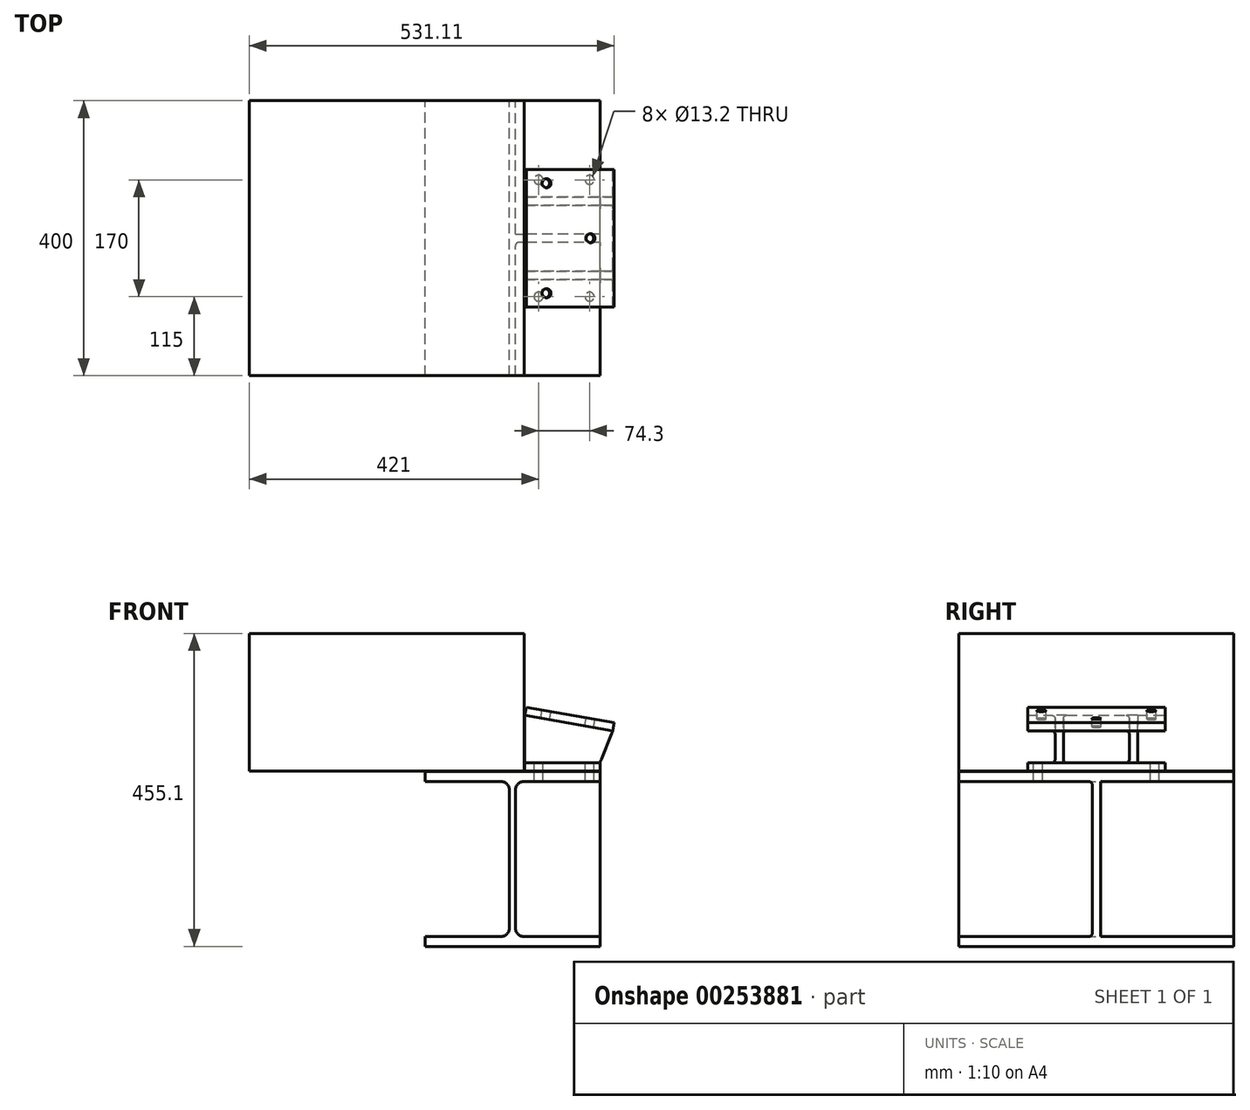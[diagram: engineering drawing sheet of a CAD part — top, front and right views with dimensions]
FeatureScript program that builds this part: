
annotation { "Feature Type Name" : "Feature", "Feature Type Description" : "" }
export const myFeature = defineFeature(function(context is Context, id is Id, definition is map)
    precondition{}
    {
        {
            var Q0;
            Q0=qCreatedBy(makeId("Front.planeOp"),FACE);
            var sketch = newSketch(context, id + "F0", { "sketchPlane" : qUnion([Q0])});
            skLineSegment(sketch, "E0.bottom", {"start": v(127.3, 127.05) * mm, "end": v(-127.3, 127.05) * mm});
            skLineSegment(sketch, "E0.top", {"start": v(127.3, -127.05) * mm, "end": v(-127.3, -127.05) * mm});
            skLineSegment(sketch, "E0.left", {"start": v(127.3, 127.05) * mm, "end": v(127.3, 112.85) * mm});
            skLineSegment(sketch, "E0.right", {"start": v(-127.3, 127.05) * mm, "end": v(-127.3, 112.85) * mm});
            skPoint(sketch, "E0.middle", {"position": v(0, 0) * mm});
            skLineSegment(sketch, "E1.0", {"start": v(127.3, 112.85) * mm, "end": v(17, 112.85) * mm});
            skLineSegment(sketch, "E2.0", {"start": v(127.3, -112.85) * mm, "end": v(17, -112.85) * mm});
            skLineSegment(sketch, "E3.0", {"start": v(4.3, 100.15) * mm, "end": v(4.3, -100.15) * mm});
            skLineSegment(sketch, "E4.0", {"start": v(-4.3, 100.15) * mm, "end": v(-4.3, -100.15) * mm});
            skLineSegment(sketch, "E5.trimOffspring", {"start": v(-17, 112.85) * mm, "end": v(-127.3, 112.85) * mm});
            skPoint(sketch, "E6.start.orphan", {"position": v(0, 127.05) * mm});
            skLineSegment(sketch, "E7.trimOffspring", {"start": v(-17, -112.85) * mm, "end": v(-127.3, -112.85) * mm});
            skPoint(sketch, "E8.trimOffspring.end.orphan", {"position": v(0, -127.05) * mm});
            skLineSegment(sketch, "E9.trimOffspring", {"start": v(-127.3, -112.85) * mm, "end": v(-127.3, -127.05) * mm});
            skLineSegment(sketch, "E10.trimOffspring", {"start": v(127.3, -112.85) * mm, "end": v(127.3, -127.05) * mm});
            skPoint(sketch, "E11.visualSharp", {"position": v(-4.3, 112.85) * mm});
            skArc(sketch, "E11.filletArc", {"start": v(-4.3, 100.15) * mm, "mid": v(-8.02, 109.13) * mm, "end": v(-17, 112.85) * mm});
            skPoint(sketch, "E12.visualSharp", {"position": v(4.3, 112.85) * mm});
            skArc(sketch, "E12.filletArc", {"start": v(17, 112.85) * mm, "mid": v(8.02, 109.13) * mm, "end": v(4.3, 100.15) * mm});
            skPoint(sketch, "E13.visualSharp", {"position": v(4.3, -112.85) * mm});
            skArc(sketch, "E13.filletArc", {"start": v(4.3, -100.15) * mm, "mid": v(8.02, -109.13) * mm, "end": v(17, -112.85) * mm});
            skPoint(sketch, "E14.visualSharp", {"position": v(-4.3, -112.85) * mm});
            skArc(sketch, "E14.filletArc", {"start": v(-17, -112.85) * mm, "mid": v(-8.02, -109.13) * mm, "end": v(-4.3, -100.15) * mm});
            skSolve(sketch);
        }
        {
            var Q0;
            Q0=makeQuery(id+"F0.imprint","IMPRINT",FACE,{"disambiguationData":[TD([[makeQuery(id+"F0.imprint","IMPRINT",EDGE,{"derivedFrom":sQuery(id+"F0.wireOp",EDGE,"E0.bottom")}),1.0]])]});
            extrude(context, id + "F1", {"entities" : qUnion([Q0]), "depth" : 400 * mm});
        }
        {
            var Q0;
            Q0=makeQuery(id+"F1.opExtrude","SWEPT_FACE",FACE,{"disambiguationData":[OSD([sQuery(id+"F0.wireOp",EDGE,"E0.bottom")])]});
            cPlane(context, id + "F2", {"entities" : qUnion([Q0]), "cplaneType" : CPlaneType.OFFSET, "offset" : 1 * mm, "width" : 150 * mm, "height" : 150 * mm});
        }
        {
            var Q0;
            Q0=qCreatedBy(id+"F2.planeOp",FACE);
            var sketch = newSketch(context, id + "F3", { "sketchPlane" : qUnion([Q0])});
            skLineSegment(sketch, "E15", {"start": v(17, 0) * mm, "end": v(17, -400) * mm});
            skLineSegment(sketch, "E16", {"start": v(17, -400) * mm, "end": v(-383, -400) * mm});
            skLineSegment(sketch, "E17", {"start": v(-383, -400) * mm, "end": v(-383, 0) * mm});
            skLineSegment(sketch, "E18", {"start": v(-383, 0) * mm, "end": v(17, 0) * mm});
            skSolve(sketch);
        }
        {
            var Q0;
            Q0=makeQuery(id+"F3.imprint","IMPRINT",FACE,{"disambiguationData":[TD([[makeQuery(id+"F3.imprint","IMPRINT",EDGE,{"derivedFrom":sQuery(id+"F3.wireOp",EDGE,"E15")}),-1.0]])]});
            extrude(context, id + "F4", {"entities" : qUnion([Q0]), "operationType" : NewBodyOperationType.ADD, "depth" : 200 * mm});
        }
        {
            var Q0;
            Q0=qCreatedBy(id+"F2.planeOp",FACE);
            var sketch = newSketch(context, id + "F5", { "sketchPlane" : qUnion([Q0])});
            skLineSegment(sketch, "E19.bottom", {"start": v(127.3, -300) * mm, "end": v(18, -300) * mm});
            skLineSegment(sketch, "E19.top", {"start": v(127.3, -100) * mm, "end": v(18, -100) * mm});
            skLineSegment(sketch, "E19.left", {"start": v(127.3, -300) * mm, "end": v(127.3, -100) * mm});
            skLineSegment(sketch, "E19.right", {"start": v(18, -300) * mm, "end": v(18, -100) * mm});
            skSolve(sketch);
        }
        {
            var Q0;
            Q0=makeQuery(id+"F5.imprint","IMPRINT",FACE,{"disambiguationData":[TD([[makeQuery(id+"F5.imprint","IMPRINT",EDGE,{"derivedFrom":sQuery(id+"F5.wireOp",EDGE,"E19.bottom")}),-1.0]])]});
            extrude(context, id + "F6", {"entities" : qUnion([Q0]), "depth" : 12 * mm});
        }
        {
            var Q0;
            Q0=makeQuery(id+"F6.opExtrude","CAP_FACE",FACE,{"disambiguationData":[OSD([sQuery(id+"F5.wireOp",EDGE,"E19.bottom"),sQuery(id+"F5.wireOp",EDGE,"E19.top"),sQuery(id+"F5.wireOp",EDGE,"E19.left"),sQuery(id+"F5.wireOp",EDGE,"E19.right")])],"isStart":false});
            var sketch = newSketch(context, id + "F7", { "sketchPlane" : qUnion([Q0])});
            skPoint(sketch, "E20", {"position": v(38, -285) * mm});
            skPoint(sketch, "E21", {"position": v(112.3, -115) * mm});
            skPoint(sketch, "E22", {"position": v(112.3, -285) * mm});
            skPoint(sketch, "E23", {"position": v(38, -115) * mm});
            skSolve(sketch);
        }
        {
            var Q0;
            Q0=sQuery(id+"F7.wireOp",VERTEX,"E20");
            var Q1;
            Q1=sQuery(id+"F7.wireOp",VERTEX,"E22");
            var Q2;
            Q2=sQuery(id+"F7.wireOp",VERTEX,"E23");
            var Q3;
            Q3=sQuery(id+"F7.wireOp",VERTEX,"E21");
            var Q4;
            Q4=makeQuery(id+"F6.opExtrude","SWEPT_BODY",BODY,{"disambiguationData":[OSD([sQuery(id+"F5.wireOp",EDGE,"E19.bottom"),sQuery(id+"F5.wireOp",EDGE,"E19.top"),sQuery(id+"F5.wireOp",EDGE,"E19.left"),sQuery(id+"F5.wireOp",EDGE,"E19.right")])]});
            hole(context, id + "F8", {"style" : HoleStyle.SIMPLE, "endStyle" : HoleEndStyle.BLIND, "standardTappedOrClearance" : lookupTablePath({ "standard" : "ISO", "fit" : "Normal", "size" : "M12", "type" : "Clearance" }), "standardBlindInLast" : lookupTablePath({ "fit" : "Standard", "standard" : "ISO", "size" : "M12", "type" : "Clearance" }), "holeDiameter" : 13.2 * mm, "holeDepth" : 12 * mm, "tappedDepth" : 12 * mm, "tapClearance" : 3, "locations" : qUnion([Q0, Q1, Q2, Q3]), "scope" : qUnion([Q4])});
        }
        {
            var Q0;
            Q0=makeQuery(id+"F1.opExtrude","SWEPT_FACE",FACE,{"disambiguationData":[OSD([sQuery(id+"F0.wireOp",EDGE,"E0.bottom")])]});
            var sketch = newSketch(context, id + "F9", { "sketchPlane" : qUnion([Q0])});
            skPoint(sketch, "E24", {"position": v(38, -285) * mm});
            skPoint(sketch, "E25", {"position": v(112.3, -285) * mm});
            skPoint(sketch, "E26", {"position": v(112.3, -115) * mm});
            skPoint(sketch, "E27", {"position": v(38, -115) * mm});
            skSolve(sketch);
        }
        {
            var Q0;
            Q0=sQuery(id+"F9.wireOp",VERTEX,"E24");
            var Q1;
            Q1=sQuery(id+"F9.wireOp",VERTEX,"E27");
            var Q2;
            Q2=sQuery(id+"F9.wireOp",VERTEX,"E25");
            var Q3;
            Q3=sQuery(id+"F9.wireOp",VERTEX,"E26");
            var Q4;
            Q4=makeQuery(id+"F1.opExtrude","SWEPT_BODY",BODY,{"disambiguationData":[OSD([sQuery(id+"F0.wireOp",EDGE,"E0.bottom"),sQuery(id+"F0.wireOp",EDGE,"E0.top"),sQuery(id+"F0.wireOp",EDGE,"E0.left"),sQuery(id+"F0.wireOp",EDGE,"E0.right"),sQuery(id+"F0.wireOp",EDGE,"E1.0"),sQuery(id+"F0.wireOp",EDGE,"E2.0"),sQuery(id+"F0.wireOp",EDGE,"E3.0"),sQuery(id+"F0.wireOp",EDGE,"E4.0"),sQuery(id+"F0.wireOp",EDGE,"E5.trimOffspring"),sQuery(id+"F0.wireOp",EDGE,"E7.trimOffspring"),sQuery(id+"F0.wireOp",EDGE,"E9.trimOffspring"),sQuery(id+"F0.wireOp",EDGE,"E10.trimOffspring"),sQuery(id+"F0.wireOp",EDGE,"E11.filletArc"),sQuery(id+"F0.wireOp",EDGE,"E12.filletArc"),sQuery(id+"F0.wireOp",EDGE,"E13.filletArc"),sQuery(id+"F0.wireOp",EDGE,"E14.filletArc")])]});
            hole(context, id + "F10", {"style" : HoleStyle.SIMPLE, "endStyle" : HoleEndStyle.BLIND, "standardTappedOrClearance" : lookupTablePath({ "standard" : "ISO", "fit" : "Normal", "size" : "M12", "type" : "Clearance" }), "standardBlindInLast" : lookupTablePath({ "fit" : "Standard", "standard" : "ISO", "size" : "M12", "type" : "Clearance" }), "holeDiameter" : 13.2 * mm, "holeDepth" : 20 * mm, "tappedDepth" : 12 * mm, "tapClearance" : 3, "locations" : qUnion([Q0, Q1, Q2, Q3]), "scope" : qUnion([Q4])});
        }
        {
            var Q0;
            Q0=makeQuery(id+"F6.opExtrude","SWEPT_FACE",FACE,{"disambiguationData":[OSD([sQuery(id+"F5.wireOp",EDGE,"E19.top")])]});
            cPlane(context, id + "F11", {"entities" : qUnion([Q0]), "cplaneType" : CPlaneType.OFFSET, "offset" : 52 * mm, "oppositeDirection" : true, "width" : 150 * mm, "height" : 150 * mm});
        }
        {
            var Q0;
            Q0=qCreatedBy(id+"F11.planeOp",FACE);
            var sketch = newSketch(context, id + "F12", { "sketchPlane" : qUnion([Q0])});
            skLineSegment(sketch, "E28", {"start": v(-18, 140.05) * mm, "end": v(-18, 209.05) * mm});
            skLineSegment(sketch, "E29", {"start": v(-18, 209.05) * mm, "end": v(-146.03, 186.48) * mm});
            skLineSegment(sketch, "E30", {"start": v(-146.03, 186.48) * mm, "end": v(-127.3, 140.05) * mm});
            skLineSegment(sketch, "E31", {"start": v(-127.3, 140.05) * mm, "end": v(-18, 140.05) * mm});
            skSolve(sketch);
        }
        {
            var Q0;
            Q0=makeQuery(id+"F6.opExtrude","SWEPT_FACE",FACE,{"disambiguationData":[OSD([sQuery(id+"F5.wireOp",EDGE,"E19.bottom")])]});
            cPlane(context, id + "F13", {"entities" : qUnion([Q0]), "cplaneType" : CPlaneType.OFFSET, "offset" : 40 * mm, "oppositeDirection" : true, "width" : 150 * mm, "height" : 150 * mm});
        }
        {
            var Q0;
            Q0=qCreatedBy(id+"F13.planeOp",FACE);
            var sketch = newSketch(context, id + "F14", { "sketchPlane" : qUnion([Q0])});
            skLineSegment(sketch, "E32", {"start": v(18, 140.05) * mm, "end": v(18, 209.05) * mm});
            skLineSegment(sketch, "E33", {"start": v(18, 209.05) * mm, "end": v(146.03, 186.48) * mm});
            skLineSegment(sketch, "E34", {"start": v(146.03, 186.48) * mm, "end": v(127.3, 140.05) * mm});
            skLineSegment(sketch, "E35", {"start": v(127.3, 140.05) * mm, "end": v(18, 140.05) * mm});
            skSolve(sketch);
        }
        {
            var Q0;
            Q0=makeQuery(id+"F12.imprint","IMPRINT",FACE,{"disambiguationData":[TD([[makeQuery(id+"F12.imprint","IMPRINT",EDGE,{"derivedFrom":sQuery(id+"F12.wireOp",EDGE,"E28")}),1.0]])]});
            var Q1;
            Q1=makeQuery(id+"F14.imprint","IMPRINT",FACE,{"disambiguationData":[TD([[makeQuery(id+"F14.imprint","IMPRINT",EDGE,{"derivedFrom":sQuery(id+"F14.wireOp",EDGE,"E32")}),-1.0]])]});
            extrude(context, id + "F15", {"entities" : qUnion([Q0, Q1]), "operationType" : NewBodyOperationType.ADD, "depth" : 12 * mm});
        }
        {
            var Q0;
            Q0=makeQuery(id+"F15.opExtrude","SWEPT_FACE",FACE,{"disambiguationData":[OSD([sQuery(id+"F14.wireOp",EDGE,"E33")])]});
            var sketch = newSketch(context, id + "F16", { "sketchPlane" : qUnion([Q0])});
            skLineSegment(sketch, "E36.bottom", {"start": v(-18.57, -300) * mm, "end": v(111.43, -300) * mm});
            skLineSegment(sketch, "E36.top", {"start": v(-18.57, -100) * mm, "end": v(111.43, -100) * mm});
            skLineSegment(sketch, "E36.left", {"start": v(-18.57, -300) * mm, "end": v(-18.57, -100) * mm});
            skLineSegment(sketch, "E36.right", {"start": v(111.43, -300) * mm, "end": v(111.43, -100) * mm});
            skSolve(sketch);
        }
        {
            var Q0;
            {var subQ0=sQuery(id+"F16.wireOp",EDGE,"E36.bottom");Q0=makeQuery(id+"F16.imprint","IMPRINT",FACE,{"disambiguationData":[TD([[makeQuery(id+"F16.imprint","IMPRINT",EDGE,{"derivedFrom":subQ0}),1.0]])]});}
            var Q1;
            {var subQ1=sQuery(id+"F14.wireOp",EDGE,"E33");var subQ2=makeQuery(id+"F15.opExtrude","CAP_EDGE",EDGE,{"disambiguationData":[OSD([subQ1])],"isStart":true});Q1=makeQuery(id+"F16.imprint","IMPRINT",FACE,{"disambiguationData":[TD([[makeQuery(id+"F16.imprint","IMPRINT",EDGE,{"derivedFrom":subQ2}),1.0]])]});}
            var Q2;
            {var subQ0=sQuery(id+"F16.wireOp",EDGE,"E36.top");Q2=makeQuery(id+"F16.imprint","IMPRINT",FACE,{"disambiguationData":[TD([[makeQuery(id+"F16.imprint","IMPRINT",EDGE,{"derivedFrom":subQ0}),-1.0]])]});}
            extrude(context, id + "F17", {"entities" : qUnion([Q0, Q1, Q2]), "operationType" : NewBodyOperationType.ADD, "depth" : 12 * mm});
        }
        {
            var Q0;
            Q0=makeQuery(id+"F15.opExtrude","CAP_EDGE",EDGE,{"disambiguationData":[OSD([sQuery(id+"F14.wireOp",EDGE,"E35")])],"isStart":true});
            var Q1;
            Q1=makeQuery(id+"F15.opExtrude","CAP_EDGE",EDGE,{"disambiguationData":[OSD([sQuery(id+"F14.wireOp",EDGE,"E35")])],"isStart":false});
            var Q2;
            Q2=makeQuery(id+"F15.opExtrude","CAP_EDGE",EDGE,{"disambiguationData":[OSD([sQuery(id+"F12.wireOp",EDGE,"E31")])],"isStart":false});
            var Q3;
            Q3=makeQuery(id+"F15.opExtrude","CAP_EDGE",EDGE,{"disambiguationData":[OSD([sQuery(id+"F12.wireOp",EDGE,"E31")])],"isStart":true});
            var Q4;
            Q4=makeQuery(id+"F15.opExtrude","CAP_EDGE",EDGE,{"disambiguationData":[OSD([sQuery(id+"F14.wireOp",EDGE,"E33")])],"isStart":true});
            var Q5;
            Q5=makeQuery(id+"F15.opExtrude","CAP_EDGE",EDGE,{"disambiguationData":[OSD([sQuery(id+"F14.wireOp",EDGE,"E33")])],"isStart":false});
            var Q6;
            Q6=makeQuery(id+"F15.opExtrude","CAP_EDGE",EDGE,{"disambiguationData":[OSD([sQuery(id+"F12.wireOp",EDGE,"E29")])],"isStart":false});
            var Q7;
            Q7=makeQuery(id+"F15.opExtrude","CAP_EDGE",EDGE,{"disambiguationData":[OSD([sQuery(id+"F12.wireOp",EDGE,"E29")])],"isStart":true});
            fillet(context, id + "F18", {"entities" : qUnion([Q0, Q1, Q2, Q3, Q4, Q5, Q6, Q7]), "radius" : 5 * mm, "tangentPropagation" : true, "allowEdgeOverflow" : false});
        }
        {
            var Q0;
            Q0=makeQuery(id+"F1.opExtrude","CAP_FACE",FACE,{"disambiguationData":[OSD([sQuery(id+"F0.wireOp",EDGE,"E0.bottom"),sQuery(id+"F0.wireOp",EDGE,"E0.top"),sQuery(id+"F0.wireOp",EDGE,"E0.left"),sQuery(id+"F0.wireOp",EDGE,"E0.right"),sQuery(id+"F0.wireOp",EDGE,"E1.0"),sQuery(id+"F0.wireOp",EDGE,"E2.0"),sQuery(id+"F0.wireOp",EDGE,"E3.0"),sQuery(id+"F0.wireOp",EDGE,"E4.0"),sQuery(id+"F0.wireOp",EDGE,"E5.trimOffspring"),sQuery(id+"F0.wireOp",EDGE,"E7.trimOffspring"),sQuery(id+"F0.wireOp",EDGE,"E9.trimOffspring"),sQuery(id+"F0.wireOp",EDGE,"E10.trimOffspring"),sQuery(id+"F0.wireOp",EDGE,"E11.filletArc"),sQuery(id+"F0.wireOp",EDGE,"E12.filletArc"),sQuery(id+"F0.wireOp",EDGE,"E13.filletArc"),sQuery(id+"F0.wireOp",EDGE,"E14.filletArc")])],"isStart":true});
            var Q1;
            Q1=makeQuery(id+"F1.opExtrude","CAP_FACE",FACE,{"disambiguationData":[OSD([sQuery(id+"F0.wireOp",EDGE,"E0.bottom"),sQuery(id+"F0.wireOp",EDGE,"E0.top"),sQuery(id+"F0.wireOp",EDGE,"E0.left"),sQuery(id+"F0.wireOp",EDGE,"E0.right"),sQuery(id+"F0.wireOp",EDGE,"E1.0"),sQuery(id+"F0.wireOp",EDGE,"E2.0"),sQuery(id+"F0.wireOp",EDGE,"E3.0"),sQuery(id+"F0.wireOp",EDGE,"E4.0"),sQuery(id+"F0.wireOp",EDGE,"E5.trimOffspring"),sQuery(id+"F0.wireOp",EDGE,"E7.trimOffspring"),sQuery(id+"F0.wireOp",EDGE,"E9.trimOffspring"),sQuery(id+"F0.wireOp",EDGE,"E10.trimOffspring"),sQuery(id+"F0.wireOp",EDGE,"E11.filletArc"),sQuery(id+"F0.wireOp",EDGE,"E12.filletArc"),sQuery(id+"F0.wireOp",EDGE,"E13.filletArc"),sQuery(id+"F0.wireOp",EDGE,"E14.filletArc")])],"isStart":false});
            cPlane(context, id + "F19", {"entities" : qUnion([Q0, Q1]), "cplaneType" : CPlaneType.MID_PLANE, "offset" : 25 * mm, "width" : 150 * mm, "height" : 150 * mm});
        }
        {
            var Q0;
            Q0=qCreatedBy(id+"F19.planeOp",FACE);
            var sketch = newSketch(context, id + "F20", { "sketchPlane" : qUnion([Q0])});
            skLineSegment(sketch, "E37", {"start": v(-127.3, 112.85) * mm, "end": v(-127.3, -112.85) * mm});
            skLineSegment(sketch, "E38", {"start": v(-127.3, -112.85) * mm, "end": v(-17, -112.85) * mm});
            skLineSegment(sketch, "E39", {"start": v(-4.3, -100.15) * mm, "end": v(-4.3, 100.15) * mm});
            skLineSegment(sketch, "E40", {"start": v(-17, 112.85) * mm, "end": v(-127.3, 112.85) * mm});
            skPoint(sketch, "E41.visualSharp", {"position": v(-4.3, 112.85) * mm});
            skArc(sketch, "E41.filletArc", {"start": v(-4.3, 100.15) * mm, "mid": v(-8.02, 109.13) * mm, "end": v(-17, 112.85) * mm});
            skPoint(sketch, "E42.visualSharp", {"position": v(-4.3, -112.85) * mm});
            skArc(sketch, "E42.filletArc", {"start": v(-17, -112.85) * mm, "mid": v(-8.02, -109.13) * mm, "end": v(-4.3, -100.15) * mm});
            skSolve(sketch);
        }
        {
            var Q0;
            Q0=makeQuery(id+"F20.imprint","IMPRINT",FACE,{"disambiguationData":[TD([[makeQuery(id+"F20.imprint","IMPRINT",EDGE,{"derivedFrom":sQuery(id+"F20.wireOp",EDGE,"E37")}),1.0]])]});
            extrude(context, id + "F21", {"entities" : qUnion([Q0]), "operationType" : NewBodyOperationType.ADD, "endBound" : BoundingType.SYMMETRIC, "depth" : 12 * mm});
        }
        {
            var Q0;
            Q0=makeQuery(id+"F21.opExtrude","CAP_EDGE",EDGE,{"disambiguationData":[OSD([sQuery(id+"F20.wireOp",EDGE,"E40")])],"isStart":false});
            var Q1;
            Q1=makeQuery(id+"F21.opExtrude","CAP_EDGE",EDGE,{"disambiguationData":[OSD([sQuery(id+"F20.wireOp",EDGE,"E39")])],"isStart":true});
            fillet(context, id + "F22", {"entities" : qUnion([Q0, Q1]), "radius" : 5 * mm, "tangentPropagation" : true, "allowEdgeOverflow" : false});
        }
        {
            var Q0;
            Q0=makeQuery(id+"F17.opExtrude","CAP_FACE",FACE,{"disambiguationData":[OSD([sQuery(id+"F16.wireOp",EDGE,"E36.bottom"),sQuery(id+"F16.wireOp",EDGE,"E36.top"),sQuery(id+"F16.wireOp",EDGE,"E36.left"),sQuery(id+"F16.wireOp",EDGE,"E36.right")])],"isStart":false});
            var sketch = newSketch(context, id + "F23", { "sketchPlane" : qUnion([Q0])});
            skPoint(sketch, "E43", {"position": v(76.43, -200) * mm});
            skPoint(sketch, "E43.positionSnap0", {"position": v(111.43, -200) * mm});
            skPoint(sketch, "E44", {"position": v(11.43, -280) * mm});
            skPoint(sketch, "E45", {"position": v(11.43, -120) * mm});
            skSolve(sketch);
        }
        {
            var Q0;
            Q0=sQuery(id+"F23.wireOp",VERTEX,"E43");
            var Q1;
            Q1=sQuery(id+"F23.wireOp",VERTEX,"E44");
            var Q2;
            Q2=sQuery(id+"F23.wireOp",VERTEX,"E45");
            var Q3;
            Q3=makeQuery(id+"F6.opExtrude","SWEPT_BODY",BODY,{"disambiguationData":[OSD([sQuery(id+"F5.wireOp",EDGE,"E19.bottom"),sQuery(id+"F5.wireOp",EDGE,"E19.top"),sQuery(id+"F5.wireOp",EDGE,"E19.left"),sQuery(id+"F5.wireOp",EDGE,"E19.right")])]});
            hole(context, id + "F24", {"style" : HoleStyle.SIMPLE, "endStyle" : HoleEndStyle.BLIND, "standardTappedOrClearance" : lookupTablePath({ "standard" : "ISO", "fit" : "Normal", "size" : "M12", "type" : "Clearance" }), "standardBlindInLast" : lookupTablePath({ "fit" : "Standard", "standard" : "ISO", "size" : "M12", "type" : "Clearance" }), "holeDiameter" : 13.2 * mm, "holeDepth" : 12 * mm, "tappedDepth" : 12 * mm, "tapClearance" : 3, "locations" : qUnion([Q0, Q1, Q2]), "scope" : qUnion([Q3])});
        }
    });
